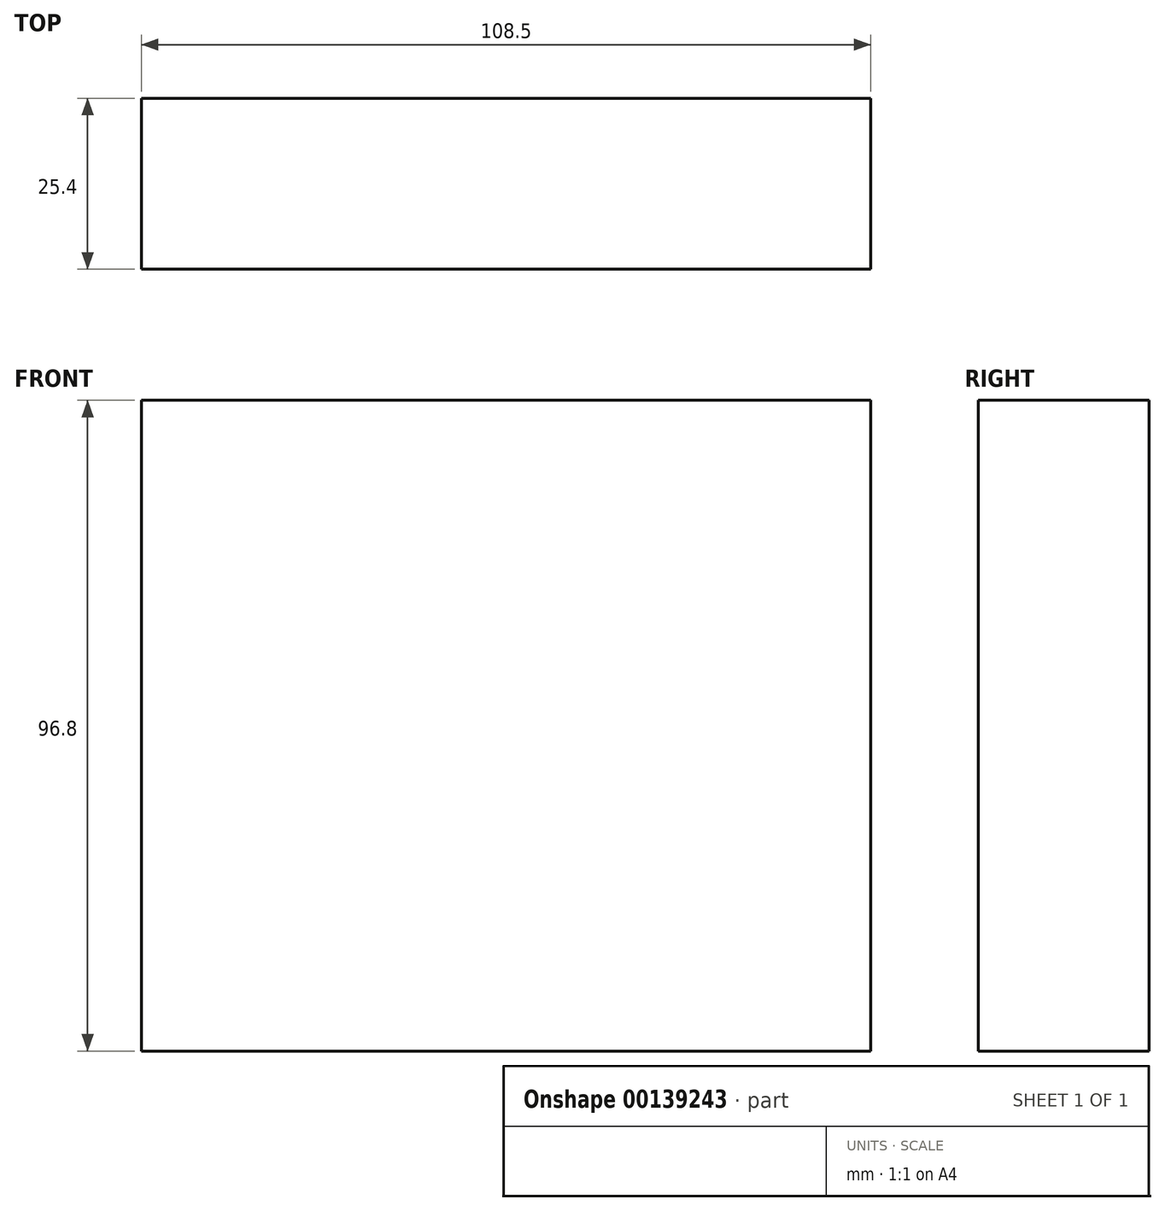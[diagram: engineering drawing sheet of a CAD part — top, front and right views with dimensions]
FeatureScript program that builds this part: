
annotation { "Feature Type Name" : "Feature", "Feature Type Description" : "" }
export const myFeature = defineFeature(function(context is Context, id is Id, definition is map)
    precondition{}
    {
        {
            var Q0;
            Q0=qCreatedBy(makeId("Front.planeOp"),FACE);
            var sketch = newSketch(context, id + "F0", { "sketchPlane" : qUnion([Q0])});
            skLineSegment(sketch, "E0.bottom", {"start": v(-56, 48.4) * mm, "end": v(52.51, 48.4) * mm});
            skLineSegment(sketch, "E0.top", {"start": v(-56, -48.4) * mm, "end": v(52.51, -48.4) * mm});
            skLineSegment(sketch, "E0.left", {"start": v(-56, 48.4) * mm, "end": v(-56, -48.4) * mm});
            skLineSegment(sketch, "E0.right", {"start": v(52.51, 48.4) * mm, "end": v(52.51, -48.4) * mm});
            skSolve(sketch);
        }
        {
            var Q0;
            Q0=makeQuery(id+"F0.imprint","IMPRINT",FACE,{"disambiguationData":[TD([[makeQuery(id+"F0.imprint","IMPRINT",EDGE,{"derivedFrom":sQuery(id+"F0.wireOp",EDGE,"E0.bottom")}),-1.0]])]});
            extrude(context, id + "F1", {"entities" : qUnion([Q0]), "depth" : 25.4 * mm});
        }
    });
